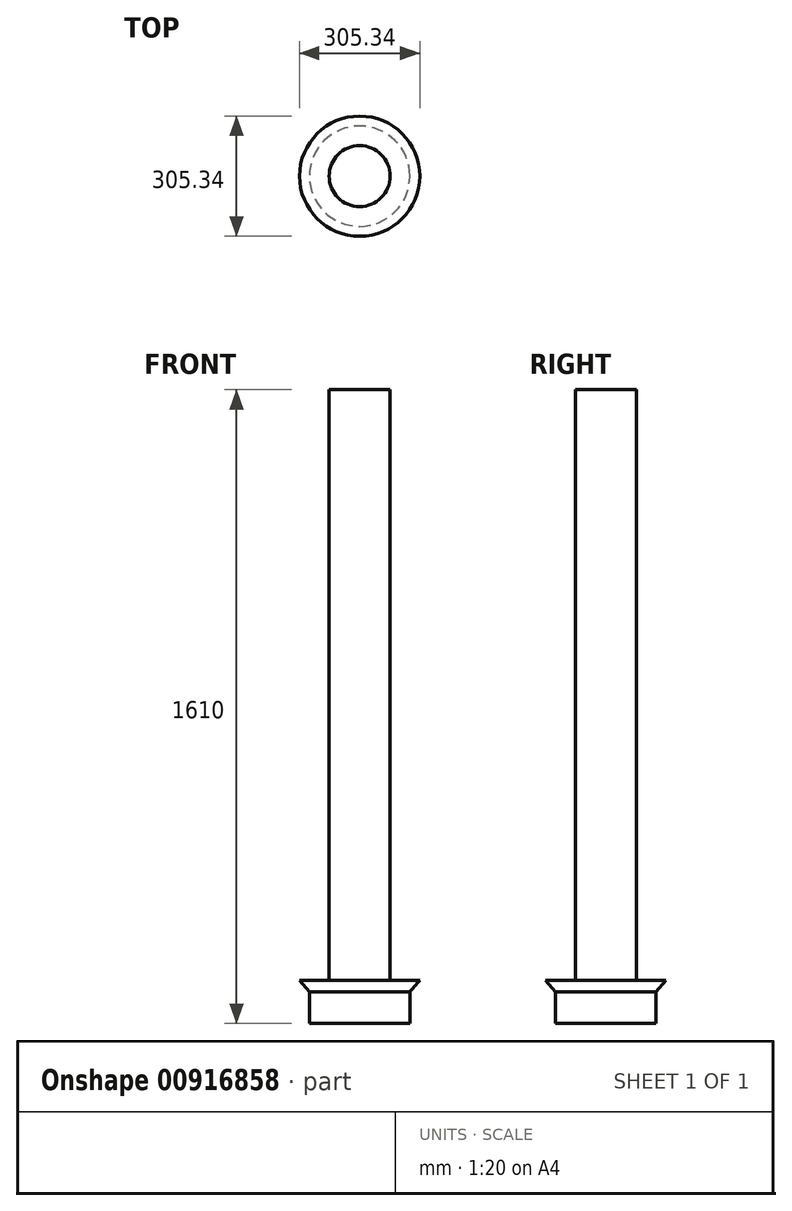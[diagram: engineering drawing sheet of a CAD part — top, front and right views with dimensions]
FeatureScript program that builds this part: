
annotation { "Feature Type Name" : "Feature", "Feature Type Description" : "" }
export const myFeature = defineFeature(function(context is Context, id is Id, definition is map)
    precondition{}
    {
        {
            var Q0;
            Q0=qCreatedBy(makeId("Top.planeOp"),FACE);
            var sketch = newSketch(context, id + "F0", { "sketchPlane" : qUnion([Q0])});
            skCircle(sketch, "E0", {"center": v(0, 0) * mm, "radius": 127.5 * mm});
            skSolve(sketch);
        }
        {
            var Q0;
            Q0 = qSketchRegion(id + "F0", true);
            extrude(context, id + "F1", {"entities" : qUnion([Q0]), "depth" : 80 * mm, "offsetDistance" : 25 * mm});
        }
        {
            var Q0;
            Q0=makeQuery(id+"F1.opExtrude","CAP_FACE",FACE,{"disambiguationData":[OSD([sQuery(id+"F0.wireOp",EDGE,"E0")])],"isStart":false});
            var sketch = newSketch(context, id + "F2", { "sketchPlane" : qUnion([Q0])});
            skCircle(sketch, "E1", {"center": v(0, 0) * mm, "radius": 127.5 * mm});
            skSolve(sketch);
        }
        {
            var Q0;
            Q0 = qSketchRegion(id + "F2", true);
            extrude(context, id + "F3", {"entities" : qUnion([Q0]), "operationType" : NewBodyOperationType.ADD, "depth" : 30 * mm, "offsetDistance" : 25 * mm, "hasDraft" : true, "draftAngle" : 40 * degree});
        }
        {
            var Q0;
            Q0=makeQuery(id+"F3.opExtrude","CAP_FACE",FACE,{"disambiguationData":[OSD([sQuery(id+"F2.wireOp",EDGE,"E1")])],"isStart":false});
            var sketch = newSketch(context, id + "F4", { "sketchPlane" : qUnion([Q0])});
            skCircle(sketch, "E2", {"center": v(0, 0) * mm, "radius": 77.5 * mm});
            skSolve(sketch);
        }
        {
            var Q0;
            Q0 = qSketchRegion(id + "F4", true);
            extrude(context, id + "F5", {"entities" : qUnion([Q0]), "operationType" : NewBodyOperationType.ADD, "depth" : 1500 * mm, "offsetDistance" : 25 * mm});
        }
    });
